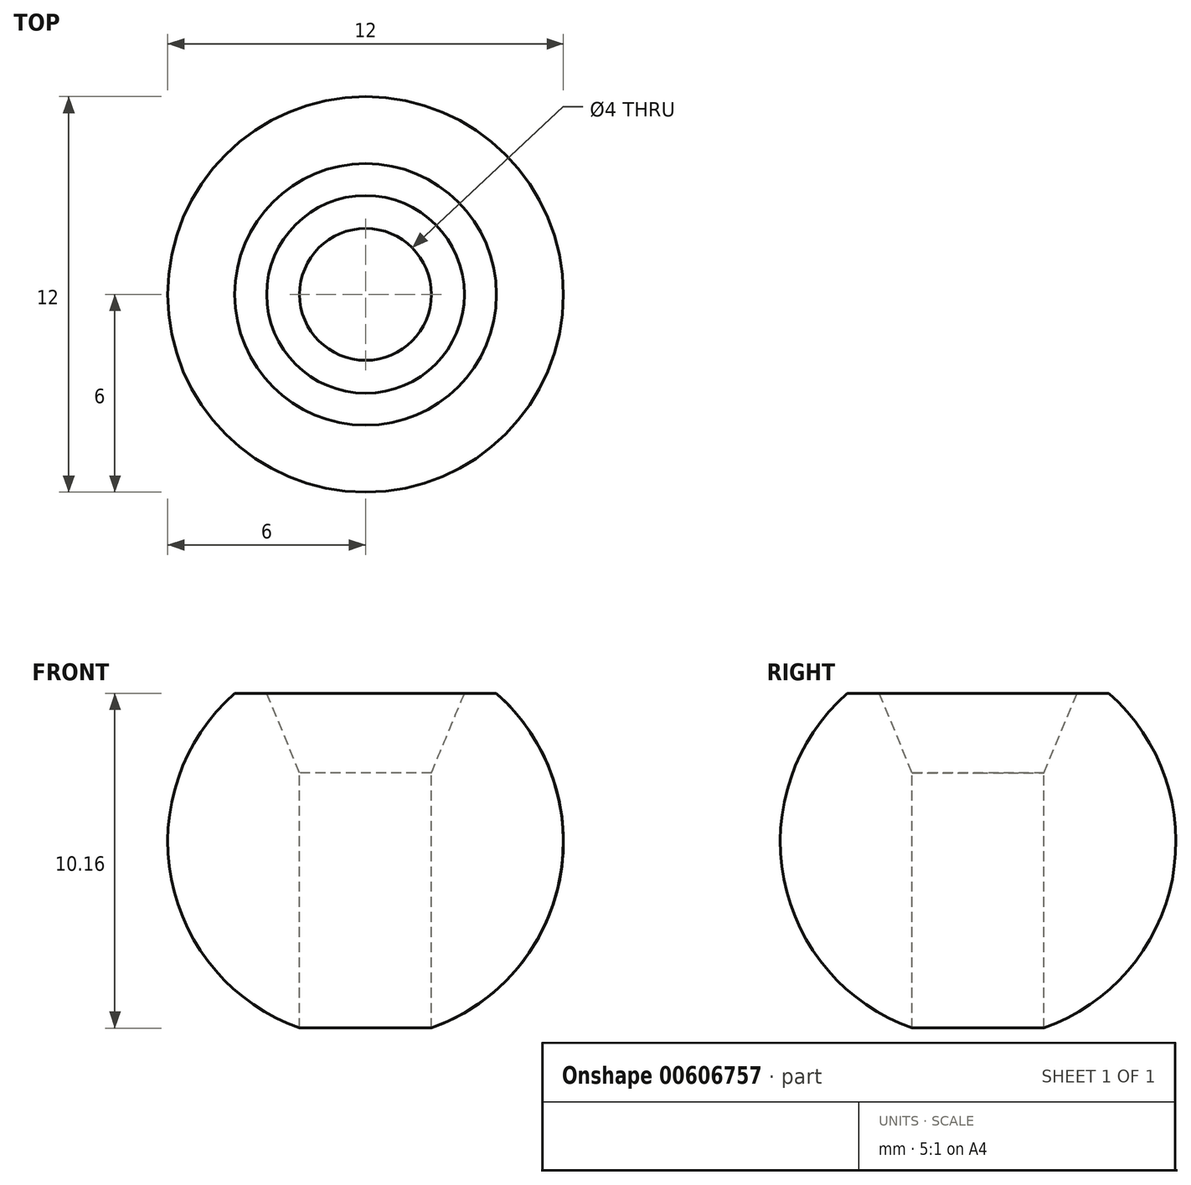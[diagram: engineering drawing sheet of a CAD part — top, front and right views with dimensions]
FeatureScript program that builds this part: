
annotation { "Feature Type Name" : "Feature", "Feature Type Description" : "" }
export const myFeature = defineFeature(function(context is Context, id is Id, definition is map)
    precondition{}
    {
        {
            var Q0;
            Q0=qCreatedBy(makeId("Front.planeOp"),FACE);
            var sketch = newSketch(context, id + "F0", { "sketchPlane" : qUnion([Q0])});
            skArc(sketch, "E0", {"start": v(0, -6) * mm, "mid": v(6, 0) * mm, "end": v(0, 6) * mm});
            skLineSegment(sketch, "E1", {"start": v(0, 9.24) * mm, "end": v(0, -10.66) * mm, "construction": true});
            skLineSegment(sketch, "E2", {"start": v(0, -6) * mm, "end": v(0, 6) * mm});
            skSolve(sketch);
        }
        {
            var Q0;
            Q0=qCreatedBy(makeId("Front.planeOp"),FACE);
            var sketch = newSketch(context, id + "F1", { "sketchPlane" : qUnion([Q0])});
            skLineSegment(sketch, "E3", {"start": v(0, 64.47) * mm, "end": v(0, -76.78) * mm, "construction": true});
            skSolve(sketch);
        }
        {
            var Q0;
            Q0=makeQuery(id+"F0.imprint","IMPRINT",FACE,{"disambiguationData":[TD([[makeQuery(id+"F0.imprint","IMPRINT",EDGE,{"derivedFrom":sQuery(id+"F0.wireOp",EDGE,"E0")}),1.0]])]});
            var Q1;
            Q1=sQuery(id+"F1.wireOp",EDGE,"E3");
            revolve(context, id + "F2", {"entities" : qUnion([Q0]), "axis" : qUnion([Q1]), "revolveType" : RevolveType.FULL});
        }
        {
            var Q0;
            Q0=qCreatedBy(makeId("Top.planeOp"),FACE);
            cPlane(context, id + "F3", {"entities" : qUnion([Q0]), "cplaneType" : CPlaneType.OFFSET, "offset" : 4.5 * mm, "width" : 150 * mm, "height" : 150 * mm});
        }
        {
            var Q0;
            Q0=qCreatedBy(id+"F3.planeOp",FACE);
            var sketch = newSketch(context, id + "F4", { "sketchPlane" : qUnion([Q0])});
            skLineSegment(sketch, "E4.bottom", {"start": v(12.38, 17.55) * mm, "end": v(-12.38, 17.55) * mm});
            skLineSegment(sketch, "E4.top", {"start": v(12.38, -17.55) * mm, "end": v(-12.38, -17.55) * mm});
            skLineSegment(sketch, "E4.left", {"start": v(12.38, 17.55) * mm, "end": v(12.38, -17.55) * mm});
            skLineSegment(sketch, "E4.right", {"start": v(-12.38, 17.55) * mm, "end": v(-12.38, -17.55) * mm});
            skPoint(sketch, "E4.middle", {"position": v(0, 0) * mm});
            skSolve(sketch);
        }
        {
            var Q0;
            Q0=makeQuery(id+"F4.imprint","IMPRINT",FACE,{"disambiguationData":[TD([[makeQuery(id+"F4.imprint","IMPRINT",EDGE,{"derivedFrom":sQuery(id+"F4.wireOp",EDGE,"E4.bottom")}),1.0]])]});
            extrude(context, id + "F5", {"entities" : qUnion([Q0]), "operationType" : NewBodyOperationType.REMOVE, "endBound" : BoundingType.THROUGH_ALL, "depth" : 25 * mm, "offsetDistance" : 25 * mm});
        }
        {
            var Q0;
            Q0=makeQuery(id+"F5.boolean.opBoolean","COPY",FACE,{"derivedFrom":makeQuery(id+"F5.opExtrude","CAP_FACE",FACE,{"disambiguationData":[OSD([sQuery(id+"F4.wireOp",EDGE,"E4.bottom"),sQuery(id+"F4.wireOp",EDGE,"E4.top"),sQuery(id+"F4.wireOp",EDGE,"E4.left"),sQuery(id+"F4.wireOp",EDGE,"E4.right")])],"isStart":true})});
            var sketch = newSketch(context, id + "F6", { "sketchPlane" : qUnion([Q0])});
            skPoint(sketch, "E5", {"position": v(0, 0) * mm});
            skSolve(sketch);
        }
        {
            var Q0;
            Q0=sQuery(id+"F6.wireOp",VERTEX,"E5");
            var Q1;
            Q1=makeQuery(id+"F2.opRevolve","SWEPT_BODY",BODY,{"disambiguationData":[OSD([sQuery(id+"F0.wireOp",EDGE,"E0"),sQuery(id+"F0.wireOp",EDGE,"E2")])]});
            hole(context, id + "F7", {"style" : HoleStyle.C_SINK, "endStyle" : HoleEndStyle.THROUGH, "holeDiameter" : 4 * mm, "cSinkDiameter" : 6 * mm, "cSinkAngle" : 45 * degree, "majorDiameter" : 5 * mm, "isTappedThrough" : true, "tappedDepth" : 12 * mm, "tapClearance" : 3, "startFromSketch" : true, "locations" : qUnion([Q0]), "scope" : qUnion([Q1])});
        }
    });
